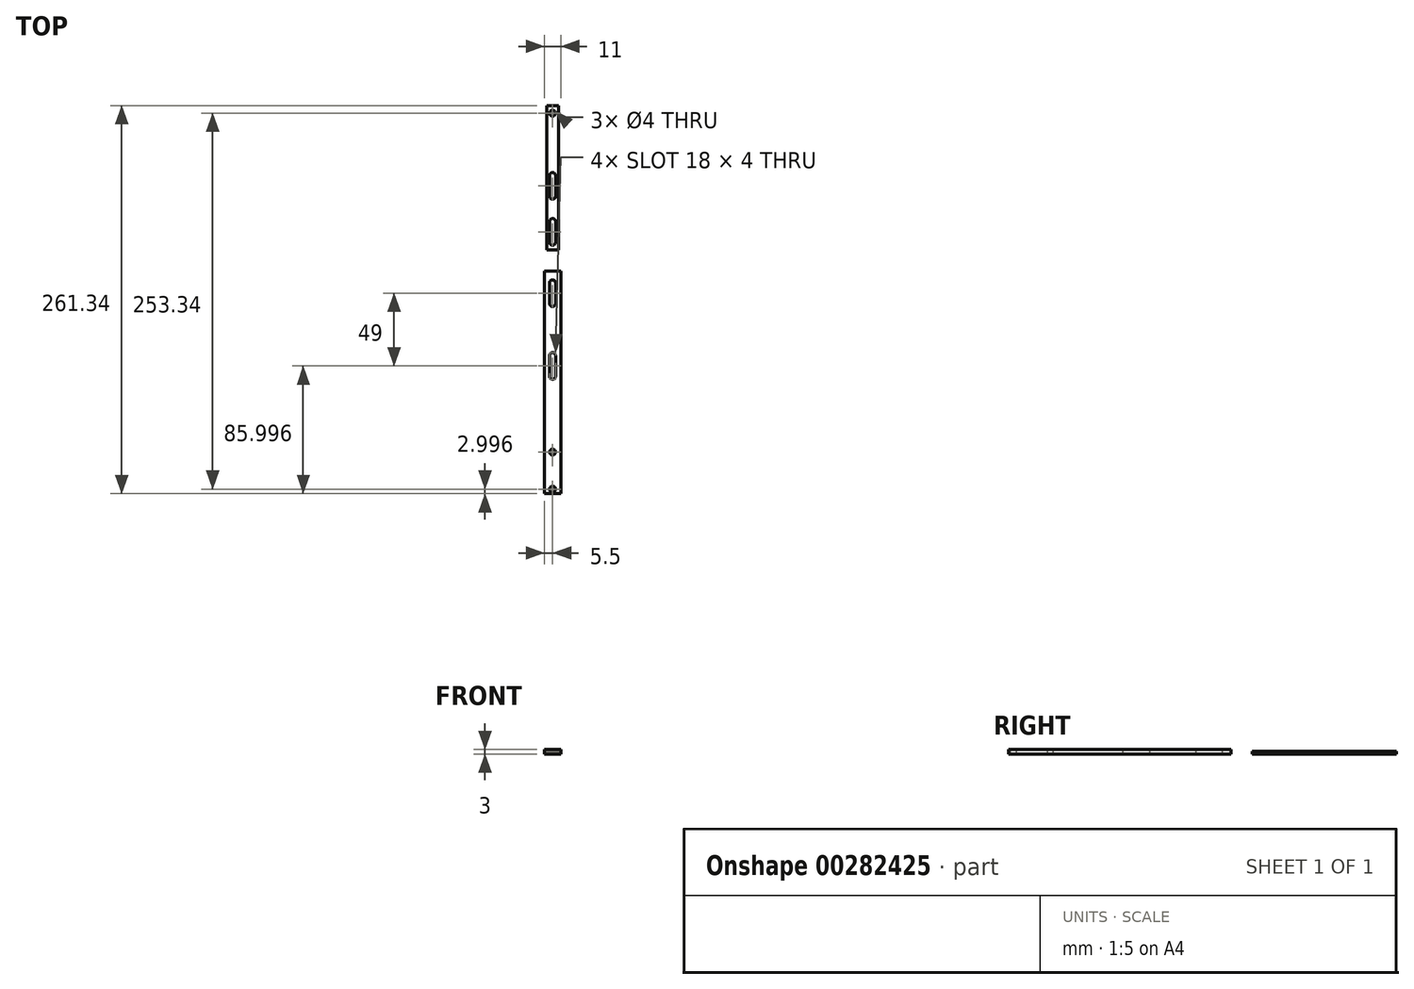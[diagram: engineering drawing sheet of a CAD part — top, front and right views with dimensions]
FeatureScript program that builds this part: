
annotation { "Feature Type Name" : "Feature", "Feature Type Description" : "" }
export const myFeature = defineFeature(function(context is Context, id is Id, definition is map)
    precondition{}
    {
        {
            var Q0;
            Q0=qCreatedBy(makeId("Top.planeOp"),FACE);
            var sketch = newSketch(context, id + "F0", { "sketchPlane" : qUnion([Q0])});
            skLineSegment(sketch, "E0.bottom", {"start": v(-4, 98.1) * mm, "end": v(4, 98.1) * mm});
            skLineSegment(sketch, "E0.top", {"start": v(-4, 1.1) * mm, "end": v(4, 1.1) * mm});
            skLineSegment(sketch, "E0.left", {"start": v(-4, 98.1) * mm, "end": v(-4, 1.1) * mm});
            skLineSegment(sketch, "E0.right", {"start": v(4, 98.1) * mm, "end": v(4, 1.1) * mm});
            skCircle(sketch, "E1", {"center": v(0, 93.1) * mm, "radius": 2 * mm});
            skLineSegment(sketch, "E2", {"start": v(0, 20.1) * mm, "end": v(0, 6.1) * mm});
            skPoint(sketch, "E3", {"position": v(0, 13.1) * mm});
            skLineSegment(sketch, "E4", {"start": v(0, 51.1) * mm, "end": v(0, 37.1) * mm});
            skPoint(sketch, "E5", {"position": v(0, 44.1) * mm});
            skArc(sketch, "E6.0.startCap", {"start": v(-2, 51.1) * mm, "mid": v(0, 53.1) * mm, "end": v(2, 51.1) * mm});
            skArc(sketch, "E6.0.endCap", {"start": v(2, 37.1) * mm, "mid": v(0, 35.1) * mm, "end": v(-2, 37.1) * mm});
            skLineSegment(sketch, "E6.0.left", {"start": v(2, 51.1) * mm, "end": v(2, 37.1) * mm});
            skLineSegment(sketch, "E6.0.right", {"start": v(-2, 51.1) * mm, "end": v(-2, 37.1) * mm});
            skArc(sketch, "E7.0.startCap", {"start": v(-2, 20.1) * mm, "mid": v(0, 22.1) * mm, "end": v(2, 20.1) * mm});
            skArc(sketch, "E7.0.endCap", {"start": v(2, 6.1) * mm, "mid": v(0, 4.1) * mm, "end": v(-2, 6.1) * mm});
            skLineSegment(sketch, "E7.0.left", {"start": v(2, 20.1) * mm, "end": v(2, 6.1) * mm});
            skLineSegment(sketch, "E7.0.right", {"start": v(-2, 20.1) * mm, "end": v(-2, 6.1) * mm});
            skSolve(sketch);
        }
        {
            var Q0;
            Q0=qCreatedBy(makeId("Top.planeOp"),FACE);
            var sketch = newSketch(context, id + "F1", { "sketchPlane" : qUnion([Q0])});
            skLineSegment(sketch, "E8.bottom", {"start": v(-5.5, -13.24) * mm, "end": v(5.5, -13.24) * mm});
            skLineSegment(sketch, "E8.top", {"start": v(-5.5, -163.24) * mm, "end": v(5.5, -163.24) * mm});
            skLineSegment(sketch, "E8.left", {"start": v(-5.5, -13.24) * mm, "end": v(-5.5, -163.24) * mm});
            skLineSegment(sketch, "E8.right", {"start": v(5.5, -13.24) * mm, "end": v(5.5, -163.24) * mm});
            skCircle(sketch, "E9", {"center": v(0, -160.24) * mm, "radius": 2 * mm});
            skCircle(sketch, "E10", {"center": v(0, -135.24) * mm, "radius": 2 * mm});
            skLineSegment(sketch, "E11", {"start": v(0, -21.24) * mm, "end": v(0, -35.24) * mm});
            skPoint(sketch, "E12", {"position": v(0, -28.24) * mm});
            skLineSegment(sketch, "E13", {"start": v(0, -70.24) * mm, "end": v(0, -84.24) * mm});
            skPoint(sketch, "E14", {"position": v(0, -77.24) * mm});
            skArc(sketch, "E15.0.startCap", {"start": v(-2, -21.24) * mm, "mid": v(0, -19.24) * mm, "end": v(2, -21.24) * mm});
            skArc(sketch, "E15.0.endCap", {"start": v(2, -35.24) * mm, "mid": v(0, -37.24) * mm, "end": v(-2, -35.24) * mm});
            skLineSegment(sketch, "E15.0.left", {"start": v(2, -21.24) * mm, "end": v(2, -35.24) * mm});
            skLineSegment(sketch, "E15.0.right", {"start": v(-2, -21.24) * mm, "end": v(-2, -35.24) * mm});
            skArc(sketch, "E15.1.startCap", {"start": v(-2, -70.24) * mm, "mid": v(0, -68.24) * mm, "end": v(2, -70.24) * mm});
            skArc(sketch, "E15.1.endCap", {"start": v(2, -84.24) * mm, "mid": v(0, -86.24) * mm, "end": v(-2, -84.24) * mm});
            skLineSegment(sketch, "E15.1.left", {"start": v(2, -70.24) * mm, "end": v(2, -84.24) * mm});
            skLineSegment(sketch, "E15.1.right", {"start": v(-2, -70.24) * mm, "end": v(-2, -84.24) * mm});
            skSolve(sketch);
        }
        {
            var Q0;
            Q0=makeQuery(id+"F0.imprint","IMPRINT",FACE,{"disambiguationData":[TD([[makeQuery(id+"F0.imprint","IMPRINT",EDGE,{"derivedFrom":sQuery(id+"F0.wireOp",EDGE,"E0.bottom")}),-1.0]])]});
            extrude(context, id + "F2", {"entities" : qUnion([Q0]), "depth" : 2 * mm});
        }
        {
            var Q0;
            Q0=makeQuery(id+"F1.imprint","IMPRINT",FACE,{"disambiguationData":[TD([[makeQuery(id+"F1.imprint","IMPRINT",EDGE,{"derivedFrom":sQuery(id+"F1.wireOp",EDGE,"E8.bottom")}),-1.0]])]});
            extrude(context, id + "F3", {"entities" : qUnion([Q0]), "depth" : 3 * mm});
        }
    });
